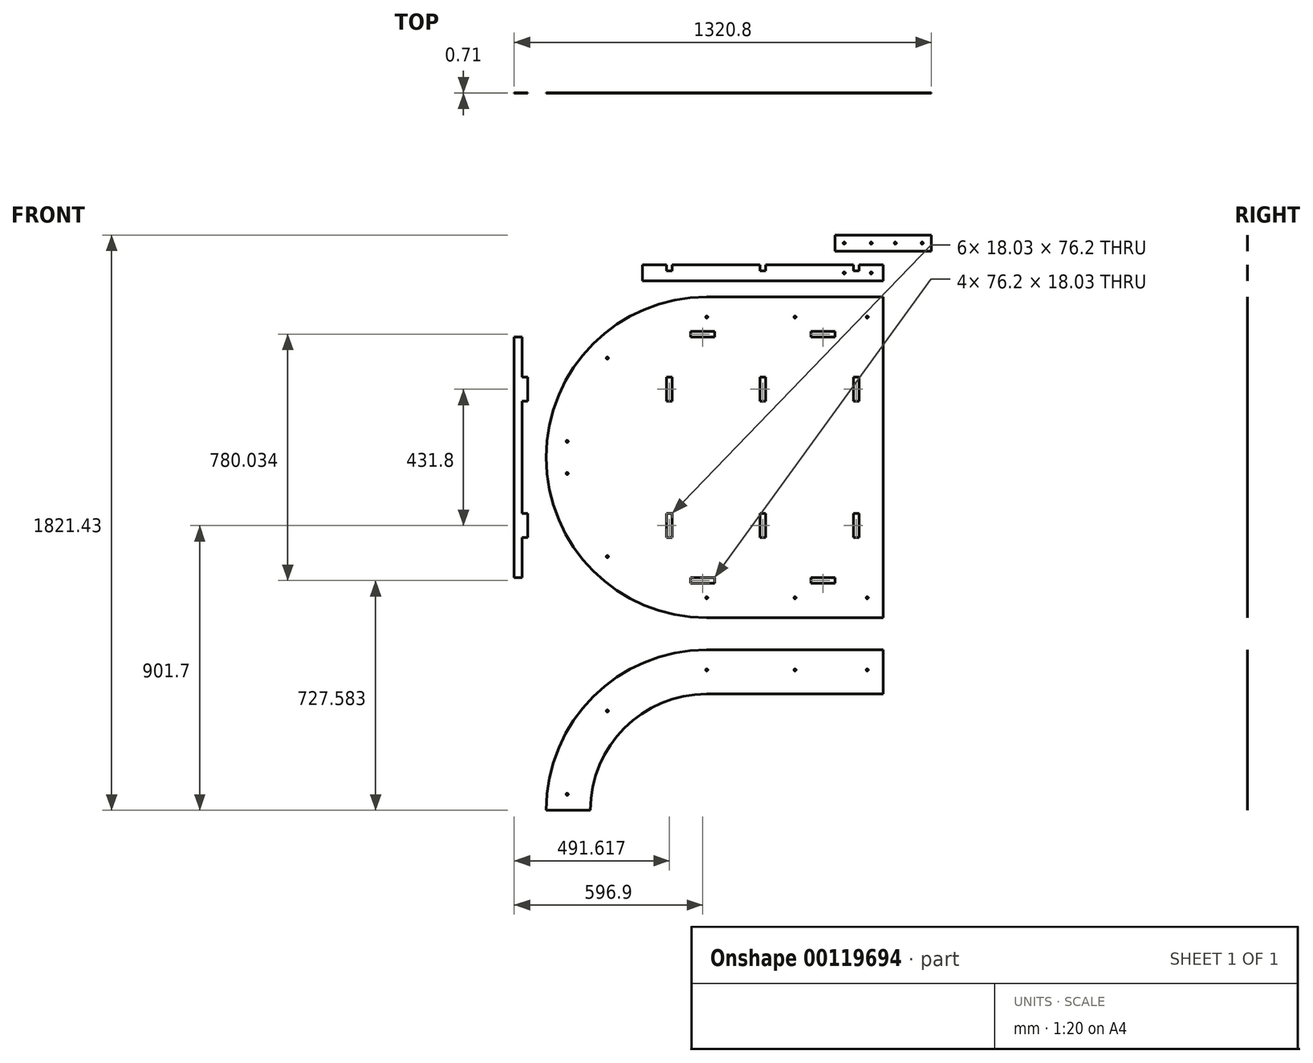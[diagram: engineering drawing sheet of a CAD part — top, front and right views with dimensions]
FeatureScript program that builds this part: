
annotation { "Feature Type Name" : "Feature", "Feature Type Description" : "" }
export const myFeature = defineFeature(function(context is Context, id is Id, definition is map)
    precondition{}
    {
        {
            assignVariable(context, id + "F0", {"name" : "thick", "anyValue" : 0.71});
        }
        {
            var Q0;
            Q0=qCreatedBy(makeId("Front.planeOp"),FACE);
            var sketch = newSketch(context, id + "F1", { "sketchPlane" : qUnion([Q0])});
            skLineSegment(sketch, "E0.bottom", {"start": v(-762, 381) * mm, "end": v(762, 381) * mm, "construction": true});
            skLineSegment(sketch, "E0.top", {"start": v(-762, -381) * mm, "end": v(762, -381) * mm, "construction": true});
            skLineSegment(sketch, "E0.left", {"start": v(-762, 381) * mm, "end": v(-762, -381) * mm, "construction": true});
            skLineSegment(sketch, "E0.right", {"start": v(762, 381) * mm, "end": v(762, -381) * mm, "construction": true});
            skPoint(sketch, "E0.middle", {"position": v(0, 0) * mm});
            skLineSegment(sketch, "E1.bottom", {"start": v(0, 508) * mm, "end": v(-558.8, 508) * mm});
            skLineSegment(sketch, "E1.top", {"start": v(0, -508) * mm, "end": v(-558.8, -508) * mm});
            skLineSegment(sketch, "E1.left", {"start": v(0, 508) * mm, "end": v(0, -508) * mm});
            skArc(sketch, "E2", {"start": v(-558.8, 508) * mm, "mid": v(-1066.8, 0) * mm, "end": v(-558.8, -508) * mm});
            skPoint(sketch, "E2.centerSnap0", {"position": v(-558.8, 508) * mm});
            skLineSegment(sketch, "E3.bottom", {"start": v(-609.6, 381) * mm, "end": v(-533.4, 381) * mm});
            skLineSegment(sketch, "E3.top", {"start": v(-609.6, 399.03) * mm, "end": v(-533.4, 399.03) * mm});
            skLineSegment(sketch, "E3.left", {"start": v(-609.6, 381) * mm, "end": v(-609.6, 399.03) * mm});
            skLineSegment(sketch, "E3.right", {"start": v(-533.4, 381) * mm, "end": v(-533.4, 399.03) * mm});
            skLineSegment(sketch, "E4.bottom", {"start": v(-228.6, 381) * mm, "end": v(-152.4, 381) * mm});
            skLineSegment(sketch, "E4.top", {"start": v(-228.6, 399.03) * mm, "end": v(-152.4, 399.03) * mm});
            skLineSegment(sketch, "E4.left", {"start": v(-228.6, 381) * mm, "end": v(-228.6, 399.03) * mm});
            skLineSegment(sketch, "E4.right", {"start": v(-152.4, 381) * mm, "end": v(-152.4, 399.03) * mm});
            skLineSegment(sketch, "E5.bottom", {"start": v(-685.8, 254) * mm, "end": v(-667.77, 254) * mm});
            skLineSegment(sketch, "E5.top", {"start": v(-685.8, 177.8) * mm, "end": v(-667.77, 177.8) * mm});
            skLineSegment(sketch, "E5.left", {"start": v(-685.8, 254) * mm, "end": v(-685.8, 177.8) * mm});
            skLineSegment(sketch, "E5.right", {"start": v(-667.77, 254) * mm, "end": v(-667.77, 177.8) * mm});
            skLineSegment(sketch, "E6.bottom", {"start": v(-390.02, 177.8) * mm, "end": v(-371.98, 177.8) * mm});
            skLineSegment(sketch, "E6.top", {"start": v(-390.02, 254) * mm, "end": v(-371.98, 254) * mm});
            skLineSegment(sketch, "E6.left", {"start": v(-390.02, 177.8) * mm, "end": v(-390.02, 254) * mm});
            skLineSegment(sketch, "E6.right", {"start": v(-371.98, 177.8) * mm, "end": v(-371.98, 254) * mm});
            skLineSegment(sketch, "E7.bottom", {"start": v(-94.23, 254) * mm, "end": v(-76.2, 254) * mm});
            skLineSegment(sketch, "E7.top", {"start": v(-94.23, 177.8) * mm, "end": v(-76.2, 177.8) * mm});
            skLineSegment(sketch, "E7.left", {"start": v(-94.23, 254) * mm, "end": v(-94.23, 177.8) * mm});
            skLineSegment(sketch, "E7.right", {"start": v(-76.2, 254) * mm, "end": v(-76.2, 177.8) * mm});
            skPoint(sketch, "E8", {"position": v(-381, 254) * mm});
            skLineSegment(sketch, "E9", {"start": v(-762, 0) * mm, "end": v(0, 0) * mm, "construction": true});
            skPoint(sketch, "E10", {"position": v(-381, 0) * mm});
            skLineSegment(sketch, "E11.MirrorCS", {"start": v(-390.02, -254) * mm, "end": v(-371.98, -254) * mm});
            skLineSegment(sketch, "E12.MirrorCS", {"start": v(-94.23, -177.8) * mm, "end": v(-76.2, -177.8) * mm});
            skLineSegment(sketch, "E13.MirrorCS", {"start": v(-228.6, -381) * mm, "end": v(-228.6, -399.03) * mm});
            skLineSegment(sketch, "E14.MirrorCS", {"start": v(-685.8, -177.8) * mm, "end": v(-667.77, -177.8) * mm});
            skLineSegment(sketch, "E15.MirrorCS", {"start": v(-390.02, -177.8) * mm, "end": v(-371.98, -177.8) * mm});
            skLineSegment(sketch, "E16.MirrorCS", {"start": v(-685.8, -254) * mm, "end": v(-667.77, -254) * mm});
            skLineSegment(sketch, "E17.MirrorCS", {"start": v(-94.23, -254) * mm, "end": v(-76.2, -254) * mm});
            skLineSegment(sketch, "E18.MirrorCS", {"start": v(-152.4, -381) * mm, "end": v(-152.4, -399.03) * mm});
            skLineSegment(sketch, "E19.MirrorCS", {"start": v(-533.4, -381) * mm, "end": v(-533.4, -399.03) * mm});
            skLineSegment(sketch, "E20.MirrorCS", {"start": v(-609.6, -381) * mm, "end": v(-609.6, -399.03) * mm});
            skLineSegment(sketch, "E21.MirrorCS", {"start": v(-228.6, -381) * mm, "end": v(-152.4, -381) * mm});
            skLineSegment(sketch, "E22.MirrorCS", {"start": v(-76.2, -254) * mm, "end": v(-76.2, -177.8) * mm});
            skLineSegment(sketch, "E23.MirrorCS", {"start": v(-228.6, -399.03) * mm, "end": v(-152.4, -399.03) * mm});
            skLineSegment(sketch, "E24.MirrorCS", {"start": v(-667.77, -254) * mm, "end": v(-667.77, -177.8) * mm});
            skLineSegment(sketch, "E25.MirrorCS", {"start": v(-371.98, -177.8) * mm, "end": v(-371.98, -254) * mm});
            skLineSegment(sketch, "E26.MirrorCS", {"start": v(-390.02, -177.8) * mm, "end": v(-390.02, -254) * mm});
            skLineSegment(sketch, "E27.MirrorCS", {"start": v(-685.8, -254) * mm, "end": v(-685.8, -177.8) * mm});
            skPoint(sketch, "E28.MirrorP", {"position": v(-381, -254) * mm});
            skLineSegment(sketch, "E29.MirrorCS", {"start": v(-609.6, -399.03) * mm, "end": v(-533.4, -399.03) * mm});
            skLineSegment(sketch, "E30.MirrorCS", {"start": v(-609.6, -381) * mm, "end": v(-533.4, -381) * mm});
            skLineSegment(sketch, "E31.MirrorCS", {"start": v(-94.23, -254) * mm, "end": v(-94.23, -177.8) * mm});
            skLineSegment(sketch, "E32.0", {"start": v(0, -444.5) * mm, "end": v(-558.8, -444.5) * mm, "construction": true});
            skArc(sketch, "E32.1", {"start": v(-558.8, 444.5) * mm, "mid": v(-1003.3, 0) * mm, "end": v(-558.8, -444.5) * mm, "construction": true});
            skLineSegment(sketch, "E32.2", {"start": v(0, 444.5) * mm, "end": v(-558.8, 444.5) * mm, "construction": true});
            skCircle(sketch, "E33", {"center": v(-558.8, 444.5) * mm, "radius": 3.3 * mm});
            skCircle(sketch, "E34", {"center": v(-50.8, 444.5) * mm, "radius": 3.3 * mm});
            skCircle(sketch, "E35", {"center": v(-279.4, 444.5) * mm, "radius": 3.3 * mm});
            skCircle(sketch, "E36", {"center": v(-1000.39, 50.8) * mm, "radius": 3.3 * mm});
            skLineSegment(sketch, "E37", {"start": v(-873.1, 314.3) * mm, "end": v(-558.8, 0) * mm, "construction": true});
            skCircle(sketch, "E38", {"center": v(-873.1, 314.3) * mm, "radius": 3.3 * mm});
            skCircle(sketch, "E39.MirrorC", {"center": v(-1000.39, -50.8) * mm, "radius": 3.3 * mm});
            skCircle(sketch, "E40.MirrorC", {"center": v(-873.1, -314.3) * mm, "radius": 3.3 * mm});
            skCircle(sketch, "E41.MirrorC", {"center": v(-558.8, -444.5) * mm, "radius": 3.3 * mm});
            skCircle(sketch, "E42.MirrorC", {"center": v(-279.4, -444.5) * mm, "radius": 3.3 * mm});
            skCircle(sketch, "E43.MirrorC", {"center": v(-50.8, -444.5) * mm, "radius": 3.3 * mm});
            skLineSegment(sketch, "E44", {"start": v(-279.4, -558.8) * mm, "end": v(0, -558.8) * mm, "construction": true});
            skLineSegment(sketch, "E45.MirrorCS", {"start": v(0, -609.6) * mm, "end": v(-558.8, -609.6) * mm});
            skArc(sketch, "E46.MirrorCS", {"start": v(-1066.8, -1117.6) * mm, "mid": v(-918.01, -758.39) * mm, "end": v(-558.8, -609.6) * mm});
            skArc(sketch, "E47.1", {"start": v(-927.1, -1117.6) * mm, "mid": v(-819.23, -857.17) * mm, "end": v(-558.8, -749.3) * mm});
            skLineSegment(sketch, "E47.2", {"start": v(0, -749.3) * mm, "end": v(-558.8, -749.3) * mm});
            skLineSegment(sketch, "E48", {"start": v(0, -609.6) * mm, "end": v(0, -749.3) * mm});
            skCircle(sketch, "E49.MirrorC", {"center": v(-558.8, -673.1) * mm, "radius": 3.3 * mm});
            skCircle(sketch, "E50.MirrorC", {"center": v(-50.8, -673.1) * mm, "radius": 3.3 * mm});
            skCircle(sketch, "E51.MirrorC", {"center": v(-279.4, -673.1) * mm, "radius": 3.3 * mm});
            skCircle(sketch, "E52.MirrorC", {"center": v(-873.1, -803.3) * mm, "radius": 3.3 * mm});
            skCircle(sketch, "E53.MirrorC", {"center": v(-1000.39, -1066.8) * mm, "radius": 3.3 * mm});
            skLineSegment(sketch, "E54", {"start": v(-927.1, -1117.6) * mm, "end": v(-1066.8, -1117.6) * mm});
            skLineSegment(sketch, "E55.bottom", {"start": v(-762, 558.8) * mm, "end": v(0, 558.8) * mm});
            skLineSegment(sketch, "E55.top", {"start": v(-762, 609.6) * mm, "end": v(0, 609.6) * mm});
            skLineSegment(sketch, "E55.left", {"start": v(-762, 558.8) * mm, "end": v(-762, 609.6) * mm});
            skLineSegment(sketch, "E55.right", {"start": v(0, 558.8) * mm, "end": v(0, 609.6) * mm});
            skLineSegment(sketch, "E56.bottom", {"start": v(-609.6, 609.6) * mm, "end": v(-533.4, 609.6) * mm});
            skLineSegment(sketch, "E56.top", {"start": v(-609.6, 627.63) * mm, "end": v(-533.4, 627.63) * mm});
            skLineSegment(sketch, "E56.left", {"start": v(-609.6, 609.6) * mm, "end": v(-609.6, 627.63) * mm});
            skLineSegment(sketch, "E56.right", {"start": v(-533.4, 609.6) * mm, "end": v(-533.4, 627.63) * mm});
            skLineSegment(sketch, "E57.bottom", {"start": v(-228.6, 609.6) * mm, "end": v(-152.4, 609.6) * mm});
            skLineSegment(sketch, "E57.top", {"start": v(-228.6, 627.63) * mm, "end": v(-152.4, 627.63) * mm});
            skLineSegment(sketch, "E57.left", {"start": v(-228.6, 609.6) * mm, "end": v(-228.6, 627.63) * mm});
            skLineSegment(sketch, "E57.right", {"start": v(-152.4, 609.6) * mm, "end": v(-152.4, 627.63) * mm});
            skLineSegment(sketch, "E58.bottom", {"start": v(-685.8, 609.6) * mm, "end": v(-667.77, 609.6) * mm});
            skLineSegment(sketch, "E58.top", {"start": v(-685.8, 590.55) * mm, "end": v(-667.77, 590.55) * mm});
            skLineSegment(sketch, "E58.left", {"start": v(-685.8, 609.6) * mm, "end": v(-685.8, 590.55) * mm});
            skLineSegment(sketch, "E58.right", {"start": v(-667.77, 609.6) * mm, "end": v(-667.77, 590.55) * mm});
            skPoint(sketch, "E59.oppositeSnap0", {"position": v(-676.78, 590.55) * mm});
            skLineSegment(sketch, "E59.bottom", {"start": v(-390.02, 609.6) * mm, "end": v(-371.98, 609.6) * mm});
            skLineSegment(sketch, "E59.top", {"start": v(-390.02, 590.55) * mm, "end": v(-371.98, 590.55) * mm});
            skLineSegment(sketch, "E59.left", {"start": v(-390.02, 609.6) * mm, "end": v(-390.02, 590.55) * mm});
            skLineSegment(sketch, "E59.right", {"start": v(-371.98, 609.6) * mm, "end": v(-371.98, 590.55) * mm});
            skLineSegment(sketch, "E60.bottom", {"start": v(-94.23, 609.6) * mm, "end": v(-76.2, 609.6) * mm});
            skLineSegment(sketch, "E60.top", {"start": v(-94.23, 590.55) * mm, "end": v(-76.2, 590.55) * mm});
            skLineSegment(sketch, "E60.left", {"start": v(-94.23, 609.6) * mm, "end": v(-94.23, 590.55) * mm});
            skLineSegment(sketch, "E60.right", {"start": v(-76.2, 609.6) * mm, "end": v(-76.2, 590.55) * mm});
            skLineSegment(sketch, "E61.bottom", {"start": v(-1143, -381) * mm, "end": v(-1168.4, -381) * mm});
            skLineSegment(sketch, "E61.top", {"start": v(-1143, 381) * mm, "end": v(-1168.4, 381) * mm});
            skLineSegment(sketch, "E61.left", {"start": v(-1143, -381) * mm, "end": v(-1143, 381) * mm});
            skLineSegment(sketch, "E61.right", {"start": v(-1168.4, -381) * mm, "end": v(-1168.4, 381) * mm});
            skLineSegment(sketch, "E62.bottom", {"start": v(-1143, 381) * mm, "end": v(-1162.05, 381) * mm});
            skLineSegment(sketch, "E62.top", {"start": v(-1143, 399.03) * mm, "end": v(-1162.05, 399.03) * mm});
            skLineSegment(sketch, "E62.left", {"start": v(-1143, 381) * mm, "end": v(-1143, 399.03) * mm});
            skLineSegment(sketch, "E62.right", {"start": v(-1162.05, 381) * mm, "end": v(-1162.05, 399.03) * mm});
            skLineSegment(sketch, "E63.bottom", {"start": v(-1143, -381) * mm, "end": v(-1162.05, -381) * mm});
            skLineSegment(sketch, "E63.top", {"start": v(-1143, -399.03) * mm, "end": v(-1162.05, -399.03) * mm});
            skLineSegment(sketch, "E63.left", {"start": v(-1143, -381) * mm, "end": v(-1143, -399.03) * mm});
            skLineSegment(sketch, "E63.right", {"start": v(-1162.05, -381) * mm, "end": v(-1162.05, -399.03) * mm});
            skLineSegment(sketch, "E64.bottom", {"start": v(-1143, 254) * mm, "end": v(-1124.97, 254) * mm});
            skLineSegment(sketch, "E64.top", {"start": v(-1143, 177.8) * mm, "end": v(-1124.97, 177.8) * mm});
            skLineSegment(sketch, "E64.left", {"start": v(-1143, 254) * mm, "end": v(-1143, 177.8) * mm});
            skLineSegment(sketch, "E64.right", {"start": v(-1124.97, 254) * mm, "end": v(-1124.97, 177.8) * mm});
            skLineSegment(sketch, "E65.bottom", {"start": v(-1143, -254) * mm, "end": v(-1124.97, -254) * mm});
            skLineSegment(sketch, "E65.top", {"start": v(-1143, -177.8) * mm, "end": v(-1124.97, -177.8) * mm});
            skLineSegment(sketch, "E65.left", {"start": v(-1143, -254) * mm, "end": v(-1143, -177.8) * mm});
            skLineSegment(sketch, "E65.right", {"start": v(-1124.97, -254) * mm, "end": v(-1124.97, -177.8) * mm});
            skCircle(sketch, "E66", {"center": v(-38.1, 584.2) * mm, "radius": 3.3 * mm});
            skPoint(sketch, "E66.centerSnap0", {"position": v(0, 584.2) * mm});
            skCircle(sketch, "E67", {"center": v(-123.32, 584.2) * mm, "radius": 3.3 * mm});
            skLineSegment(sketch, "E68", {"start": v(-152.4, 590.55) * mm, "end": v(-94.23, 590.55) * mm, "construction": true});
            skPoint(sketch, "E69", {"position": v(-123.32, 590.55) * mm});
            skLineSegment(sketch, "E70.bottom", {"start": v(-152.4, 653.03) * mm, "end": v(152.4, 653.03) * mm});
            skLineSegment(sketch, "E70.top", {"start": v(-152.4, 703.83) * mm, "end": v(152.4, 703.83) * mm});
            skLineSegment(sketch, "E70.left", {"start": v(-152.4, 653.03) * mm, "end": v(-152.4, 703.83) * mm});
            skLineSegment(sketch, "E70.right", {"start": v(152.4, 653.03) * mm, "end": v(152.4, 703.83) * mm});
            skLineSegment(sketch, "E71", {"start": v(0, 653.03) * mm, "end": v(0, 609.6) * mm, "construction": true});
            skLineSegment(sketch, "E72", {"start": v(0, 631.32) * mm, "end": v(-76.2, 631.32) * mm, "construction": true});
            skCircle(sketch, "E73.MirrorC", {"center": v(-123.32, 678.43) * mm, "radius": 3.3 * mm});
            skCircle(sketch, "E74.MirrorC", {"center": v(-38.1, 678.43) * mm, "radius": 3.3 * mm});
            skCircle(sketch, "E75.MirrorC", {"center": v(38.1, 678.43) * mm, "radius": 3.3 * mm});
            skCircle(sketch, "E76.MirrorC", {"center": v(123.32, 678.43) * mm, "radius": 3.3 * mm});
            skSolve(sketch);
        }
        {
            var Q0;
            Q0=makeQuery(id+"F1.imprint","IMPRINT",FACE,{"disambiguationData":[TD([[makeQuery(id+"F1.imprint","IMPRINT",EDGE,{"derivedFrom":sQuery(id+"F1.wireOp",EDGE,"E62.bottom")}),-1.0]])]});
            var Q1;
            Q1=makeQuery(id+"F1.imprint","IMPRINT",FACE,{"disambiguationData":[TD([[makeQuery(id+"F1.imprint","IMPRINT",EDGE,{"derivedFrom":sQuery(id+"F1.wireOp",EDGE,"E61.bottom")}),-1.0]])]});
            var Q2;
            Q2=makeQuery(id+"F1.imprint","IMPRINT",FACE,{"disambiguationData":[TD([[makeQuery(id+"F1.imprint","IMPRINT",EDGE,{"derivedFrom":sQuery(id+"F1.wireOp",EDGE,"E64.bottom")}),-1.0]])]});
            var Q3;
            Q3=makeQuery(id+"F1.imprint","IMPRINT",FACE,{"disambiguationData":[TD([[makeQuery(id+"F1.imprint","IMPRINT",EDGE,{"derivedFrom":sQuery(id+"F1.wireOp",EDGE,"E63.bottom")}),1.0]])]});
            var Q4;
            Q4=makeQuery(id+"F1.imprint","IMPRINT",FACE,{"disambiguationData":[TD([[makeQuery(id+"F1.imprint","IMPRINT",EDGE,{"derivedFrom":sQuery(id+"F1.wireOp",EDGE,"E65.bottom")}),1.0]])]});
            var Q5;
            Q5=makeQuery(id+"F1.imprint","IMPRINT",FACE,{"disambiguationData":[TD([[makeQuery(id+"F1.imprint","IMPRINT",EDGE,{"derivedFrom":sQuery(id+"F1.wireOp",EDGE,"E1.bottom")}),1.0]])]});
            var Q6;
            Q6=makeQuery(id+"F1.imprint","IMPRINT",FACE,{"disambiguationData":[TD([[makeQuery(id+"F1.imprint","IMPRINT",EDGE,{"derivedFrom":sQuery(id+"F1.wireOp",EDGE,"E45.MirrorCS")}),1.0]])]});
            var Q7;
            Q7=makeQuery(id+"F1.imprint","IMPRINT",FACE,{"disambiguationData":[TD([[makeQuery(id+"F1.imprint","IMPRINT",EDGE,{"derivedFrom":sQuery(id+"F1.wireOp",EDGE,"E55.bottom")}),1.0]])]});
            var Q8;
            Q8=makeQuery(id+"F1.imprint","IMPRINT",FACE,{"disambiguationData":[TD([[makeQuery(id+"F1.imprint","IMPRINT",EDGE,{"derivedFrom":sQuery(id+"F1.wireOp",EDGE,"E56.bottom")}),1.0]])]});
            var Q9;
            Q9=makeQuery(id+"F1.imprint","IMPRINT",FACE,{"disambiguationData":[TD([[makeQuery(id+"F1.imprint","IMPRINT",EDGE,{"derivedFrom":sQuery(id+"F1.wireOp",EDGE,"E57.bottom")}),1.0]])]});
            var Q10;
            Q10=makeQuery(id+"F1.imprint","IMPRINT",FACE,{"disambiguationData":[TD([[makeQuery(id+"F1.imprint","IMPRINT",EDGE,{"derivedFrom":sQuery(id+"F1.wireOp",EDGE,"E70.bottom")}),1.0]])]});
            extrude(context, id + "F2", {"entities" : qUnion([Q0, Q1, Q2, Q3, Q4, Q5, Q6, Q7, Q8, Q9, Q10]), "depth" : (getVariable(context, 'thick')) * mm});
        }
    });
